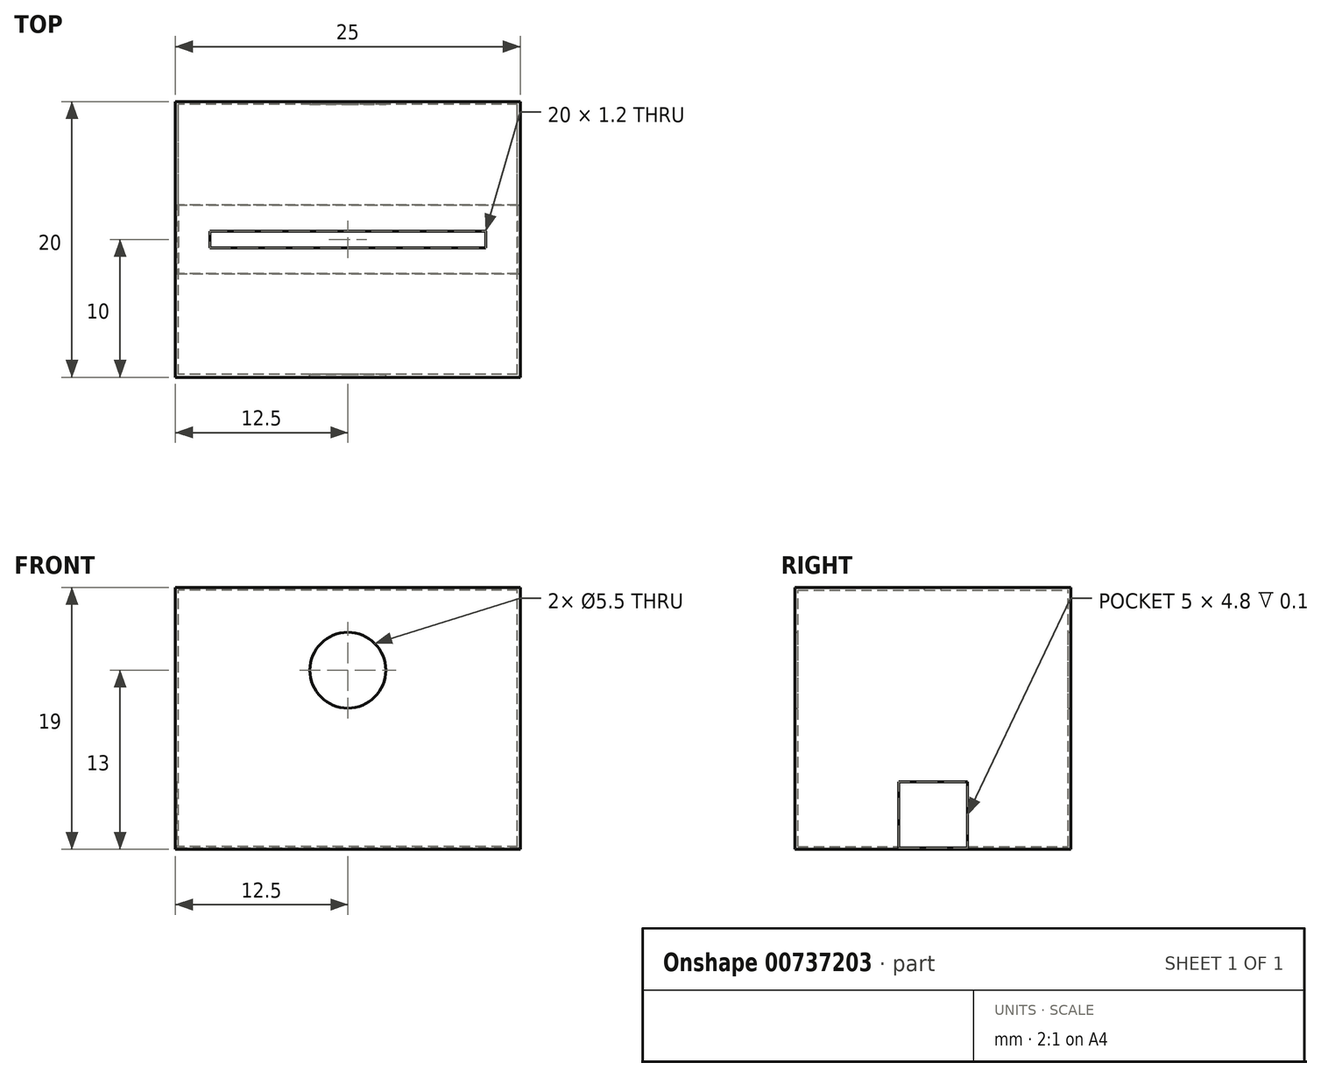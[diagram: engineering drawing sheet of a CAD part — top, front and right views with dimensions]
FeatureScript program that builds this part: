
annotation { "Feature Type Name" : "Feature", "Feature Type Description" : "" }
export const myFeature = defineFeature(function(context is Context, id is Id, definition is map)
    precondition{}
    {
        {
            var Q0;
            Q0=qCreatedBy(makeId("Front.planeOp"),FACE);
            var sketch = newSketch(context, id + "F0", { "sketchPlane" : qUnion([Q0])});
            skLineSegment(sketch, "E0.bottom", {"start": v(0, 0) * mm, "end": v(-25, 0) * mm});
            skLineSegment(sketch, "E0.top", {"start": v(0, 19) * mm, "end": v(-25, 19) * mm});
            skLineSegment(sketch, "E0.left", {"start": v(0, 0) * mm, "end": v(0, 19) * mm});
            skLineSegment(sketch, "E0.right", {"start": v(-25, 0) * mm, "end": v(-25, 19) * mm});
            skSolve(sketch);
        }
        {
            var Q0;
            Q0=makeQuery(id+"F0.imprint","IMPRINT",FACE,{"disambiguationData":[TD([[makeQuery(id+"F0.imprint","IMPRINT",EDGE,{"derivedFrom":sQuery(id+"F0.wireOp",EDGE,"E0.bottom")}),-1.0]])]});
            extrude(context, id + "F1", {"entities" : qUnion([Q0]), "depth" : 20 * mm, "offsetDistance" : 25 * mm});
        }
        {
            var Q0;
            Q0=qCreatedBy(makeId("Front.planeOp"),FACE);
            var sketch = newSketch(context, id + "F2", { "sketchPlane" : qUnion([Q0])});
            skCircle(sketch, "E1", {"center": v(-12.5, 13) * mm, "radius": 2.75 * mm});
            skSolve(sketch);
        }
        {
            var Q0;
            Q0=makeQuery(id+"F1.opExtrude","CAP_FACE",FACE,{"disambiguationData":[OSD([sQuery(id+"F0.wireOp",EDGE,"E0.bottom"),sQuery(id+"F0.wireOp",EDGE,"E0.top"),sQuery(id+"F0.wireOp",EDGE,"E0.left"),sQuery(id+"F0.wireOp",EDGE,"E0.right")])],"isStart":true});
            var Q1;
            Q1=makeQuery(id+"F1.opExtrude","SWEPT_BODY",BODY,{"disambiguationData":[OSD([sQuery(id+"F0.wireOp",EDGE,"E0.bottom"),sQuery(id+"F0.wireOp",EDGE,"E0.top"),sQuery(id+"F0.wireOp",EDGE,"E0.left"),sQuery(id+"F0.wireOp",EDGE,"E0.right")])]});
            shell(context, id + "F3", {"isHollow" : true, "entities" : qUnion([Q0]), "parts" : qUnion([Q1]), "thickness" : 0.2 * mm});
        }
        {
            var Q0;
            Q0=makeQuery(id+"F2.imprint","IMPRINT",FACE,{"disambiguationData":[TD([[makeQuery(id+"F2.imprint","IMPRINT",EDGE,{"derivedFrom":sQuery(id+"F2.wireOp",EDGE,"E1")}),1.0]])]});
            extrude(context, id + "F4", {"entities" : qUnion([Q0]), "operationType" : NewBodyOperationType.REMOVE, "oppositeDirection" : true, "depth" : -25 * mm, "offsetDistance" : 25 * mm});
        }
        {
            var Q0;
            Q0=makeQuery(id+"F1.opExtrude","SWEPT_FACE",FACE,{"disambiguationData":[OSD([sQuery(id+"F0.wireOp",EDGE,"E0.top")])]});
            var sketch = newSketch(context, id + "F5", { "sketchPlane" : qUnion([Q0])});
            skLineSegment(sketch, "E2.bottom", {"start": v(-22.5, -9.4) * mm, "end": v(-2.5, -9.4) * mm});
            skLineSegment(sketch, "E2.top", {"start": v(-22.5, -10.6) * mm, "end": v(-2.5, -10.6) * mm});
            skLineSegment(sketch, "E2.left", {"start": v(-22.5, -9.4) * mm, "end": v(-22.5, -10.6) * mm});
            skLineSegment(sketch, "E2.right", {"start": v(-2.5, -9.4) * mm, "end": v(-2.5, -10.6) * mm});
            skSolve(sketch);
        }
        {
            var Q0;
            Q0 = qSketchRegion(id + "F5", true);
            extrude(context, id + "F6", {"entities" : qUnion([Q0]), "operationType" : NewBodyOperationType.REMOVE, "oppositeDirection" : true, "depth" : 1 * mm, "offsetDistance" : 25 * mm});
        }
        {
            var Q0;
            Q0=makeQuery(id+"F1.opExtrude","SWEPT_FACE",FACE,{"disambiguationData":[OSD([sQuery(id+"F0.wireOp",EDGE,"E0.left")])]});
            var sketch = newSketch(context, id + "F7", { "sketchPlane" : qUnion([Q0])});
            skLineSegment(sketch, "E3.bottom", {"start": v(-12.5, 4.9) * mm, "end": v(-7.5, 4.9) * mm});
            skLineSegment(sketch, "E3.top", {"start": v(-12.5, 0.1) * mm, "end": v(-7.5, 0.1) * mm});
            skLineSegment(sketch, "E3.left", {"start": v(-12.5, 4.9) * mm, "end": v(-12.5, 0.1) * mm});
            skLineSegment(sketch, "E3.right", {"start": v(-7.5, 4.9) * mm, "end": v(-7.5, 0.1) * mm});
            skSolve(sketch);
        }
        {
            var Q0;
            Q0 = qSketchRegion(id + "F7", true);
            extrude(context, id + "F8", {"entities" : qUnion([Q0]), "operationType" : NewBodyOperationType.REMOVE, "oppositeDirection" : true, "depth" : 24.9 * mm, "offsetDistance" : 25 * mm});
        }
    });
